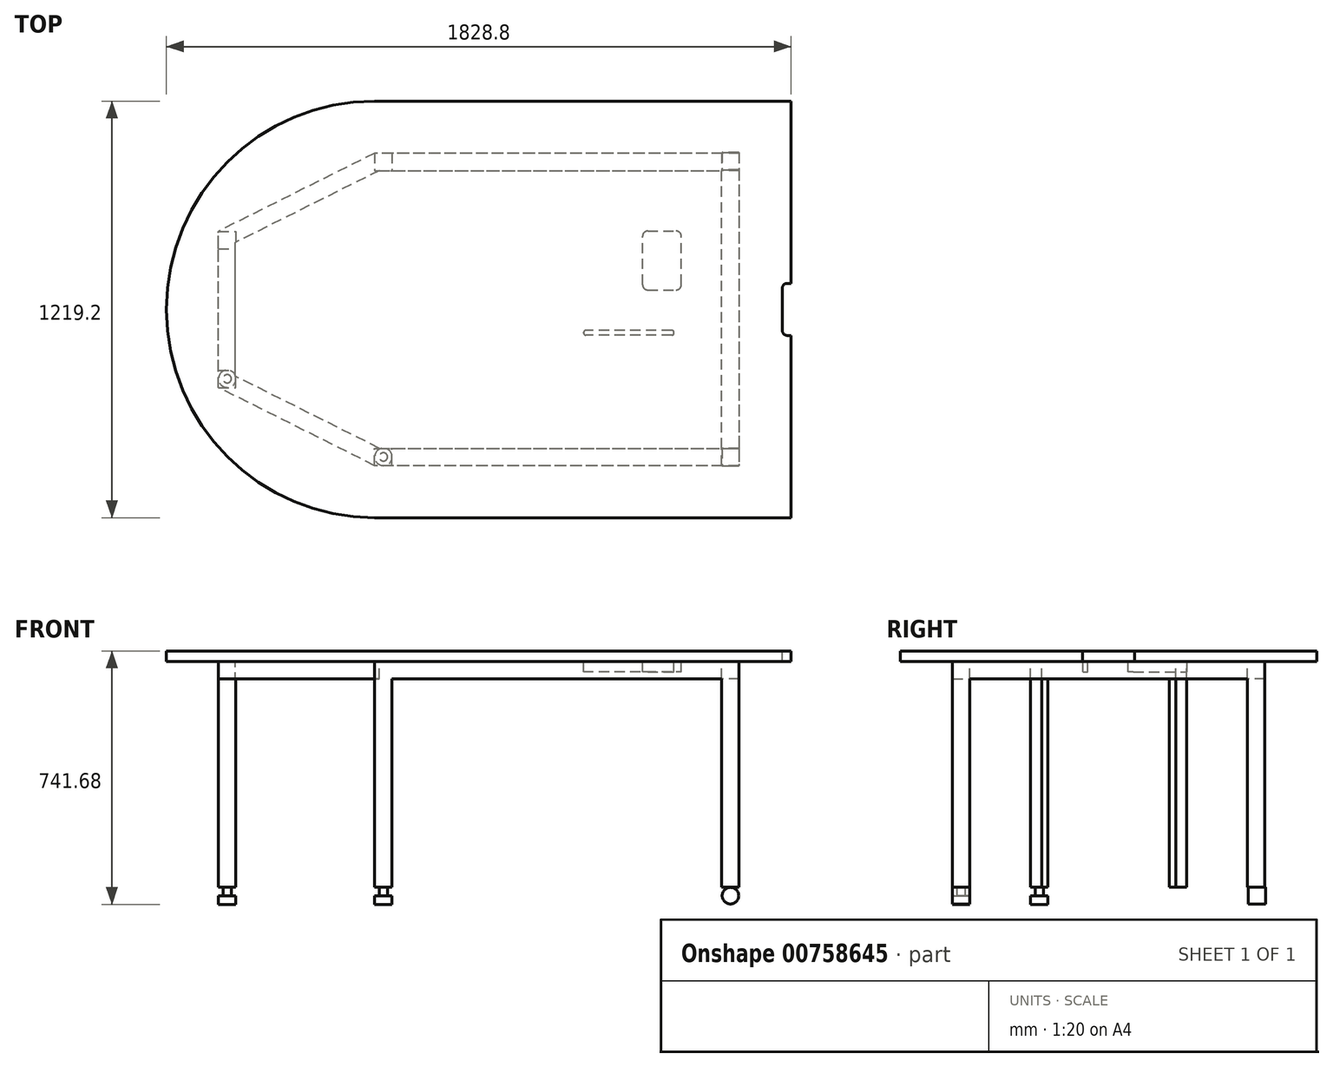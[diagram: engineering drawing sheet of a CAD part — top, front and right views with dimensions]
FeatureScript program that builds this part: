
annotation { "Feature Type Name" : "Feature", "Feature Type Description" : "" }
export const myFeature = defineFeature(function(context is Context, id is Id, definition is map)
    precondition{}
    {
        {
            var Q0;
            Q0=qCreatedBy(makeId("Top.planeOp"),FACE);
            var sketch = newSketch(context, id + "F0", { "sketchPlane" : qUnion([Q0])});
            skLineSegment(sketch, "E0.bottom", {"start": v(0, 0) * mm, "end": v(1219.2, 0) * mm});
            skLineSegment(sketch, "E0.top", {"start": v(0, -1219.2) * mm, "end": v(1219.2, -1219.2) * mm});
            skLineSegment(sketch, "E0.left", {"start": v(0, 0) * mm, "end": v(0, -1219.2) * mm});
            skCircle(sketch, "E1", {"center": v(0, -609.6) * mm, "radius": 609.6 * mm});
            skPoint(sketch, "E2.startSnap0", {"position": v(609.6, -1219.2) * mm});
            skLineSegment(sketch, "E3", {"start": v(1276.56, -609.6) * mm, "end": v(1133.94, -609.6) * mm, "construction": true});
            skPoint(sketch, "E3.startSnap0", {"position": v(1219.2, -609.6) * mm});
            skLineSegment(sketch, "E4", {"start": v(1219.2, -533.4) * mm, "end": v(1206.5, -533.4) * mm});
            skLineSegment(sketch, "E5", {"start": v(1193.8, -546.1) * mm, "end": v(1193.8, -609.6) * mm});
            skPoint(sketch, "E6.visualSharp", {"position": v(1193.8, -533.4) * mm});
            skArc(sketch, "E6.filletArc", {"start": v(1206.5, -533.4) * mm, "mid": v(1197.52, -537.12) * mm, "end": v(1193.8, -546.1) * mm});
            skLineSegment(sketch, "E7.MirrorCS", {"start": v(1193.8, -673.1) * mm, "end": v(1193.8, -609.6) * mm});
            skArc(sketch, "E8.MirrorCS", {"start": v(1206.5, -685.8) * mm, "mid": v(1197.52, -682.08) * mm, "end": v(1193.8, -673.1) * mm});
            skLineSegment(sketch, "E9.MirrorCS", {"start": v(1219.2, -685.8) * mm, "end": v(1206.5, -685.8) * mm});
            skLineSegment(sketch, "E10", {"start": v(1219.2, 0) * mm, "end": v(1219.2, -533.4) * mm});
            skLineSegment(sketch, "E11", {"start": v(1219.2, -685.8) * mm, "end": v(1219.2, -1219.2) * mm});
            skSolve(sketch);
        }
        {
            var Q0;
            {var subQ0=sQuery(id+"F0.wireOp",EDGE,"E0.bottom");Q0=makeQuery(id+"F0.imprint","IMPRINT",FACE,{"disambiguationData":[TD([[makeQuery(id+"F0.imprint","IMPRINT",EDGE,{"derivedFrom":subQ0}),-1.0]])]});}
            var Q1;
            {var subQ0=sQuery(id+"F0.wireOp",EDGE,"E0.left");Q1=makeQuery(id+"F0.imprint","IMPRINT",FACE,{"disambiguationData":[TD([[makeQuery(id+"F0.imprint","IMPRINT",EDGE,{"derivedFrom":subQ0}),-1.0]])]});}
            var Q2;
            {var subQ0=sQuery(id+"F0.wireOp",EDGE,"E0.left");Q2=makeQuery(id+"F0.imprint","IMPRINT",FACE,{"disambiguationData":[TD([[makeQuery(id+"F0.imprint","IMPRINT",EDGE,{"derivedFrom":subQ0}),1.0]])]});}
            extrude(context, id + "F1", {"entities" : qUnion([Q0, Q1, Q2]), "oppositeDirection" : true, "depth" : 30.48 * mm, "offsetDistance" : 30.48 * mm});
        }
        {
            var Q0;
            Q0=makeQuery(id+"F1.opExtrude","CAP_FACE",FACE,{"disambiguationData":[OSD([sQuery(id+"F0.wireOp",EDGE,"E0.bottom"),sQuery(id+"F0.wireOp",EDGE,"E0.top"),sQuery(id+"F0.wireOp",EDGE,"E0.right"),sQuery(id+"F0.wireOp",EDGE,"E1")])],"isStart":false});
            var sketch = newSketch(context, id + "F2", { "sketchPlane" : qUnion([Q0])});
            skPoint(sketch, "E12.startSnap0", {"position": v(1219.2, 609.6) * mm});
            skLineSegment(sketch, "E13.0", {"start": v(0, 1219.2) * mm, "end": v(1219.2, 1219.2) * mm});
            skPoint(sketch, "E14", {"position": v(0, 1066.8) * mm});
            skLineSegment(sketch, "E15", {"start": v(1066.8, 609.6) * mm, "end": v(1066.8, 1066.8) * mm});
            skLineSegment(sketch, "E16", {"start": v(1066.8, 1066.8) * mm, "end": v(0, 1066.8) * mm});
            skLineSegment(sketch, "E17", {"start": v(13.53, 1016) * mm, "end": v(1016, 1016) * mm});
            skLineSegment(sketch, "E18", {"start": v(1016, 1016) * mm, "end": v(1016, 609.6) * mm});
            skPoint(sketch, "E19", {"position": v(-457.2, 609.6) * mm});
            skPoint(sketch, "E20", {"position": v(-457.2, 838.2) * mm});
            skLineSegment(sketch, "E21", {"start": v(0, 1066.8) * mm, "end": v(-457.2, 838.2) * mm});
            skLineSegment(sketch, "E22", {"start": v(-457.2, 838.2) * mm, "end": v(-457.2, 609.6) * mm});
            skLineSegment(sketch, "E23", {"start": v(-407.87, 609.6) * mm, "end": v(-407.87, 805.3) * mm});
            skLineSegment(sketch, "E24", {"start": v(13.53, 1016) * mm, "end": v(-407.87, 805.3) * mm});
            skLineSegment(sketch, "E25.MirrorCS", {"start": v(1066.8, 609.6) * mm, "end": v(1066.8, 152.4) * mm});
            skLineSegment(sketch, "E26.MirrorCS", {"start": v(0, 152.4) * mm, "end": v(-457.2, 381) * mm});
            skLineSegment(sketch, "E27.MirrorCS", {"start": v(13.53, 203.2) * mm, "end": v(-407.87, 413.9) * mm});
            skLineSegment(sketch, "E28.MirrorCS", {"start": v(-407.87, 609.6) * mm, "end": v(-407.87, 413.9) * mm});
            skLineSegment(sketch, "E29.MirrorCS", {"start": v(-457.2, 381) * mm, "end": v(-457.2, 609.6) * mm});
            skLineSegment(sketch, "E30.MirrorCS", {"start": v(1016, 203.2) * mm, "end": v(1016, 609.6) * mm});
            skPoint(sketch, "E31.MirrorP", {"position": v(-457.2, 381) * mm});
            skLineSegment(sketch, "E32.MirrorCS", {"start": v(13.53, 203.2) * mm, "end": v(1016, 203.2) * mm});
            skLineSegment(sketch, "E33.MirrorCS", {"start": v(1066.8, 152.4) * mm, "end": v(0, 152.4) * mm});
            skSolve(sketch);
        }
        {
            var Q0;
            Q0=makeQuery(id+"F2.imprint","IMPRINT",FACE,{"disambiguationData":[TD([[makeQuery(id+"F2.imprint","IMPRINT",EDGE,{"derivedFrom":sQuery(id+"F2.wireOp",EDGE,"E15")}),1.0]])]});
            extrude(context, id + "F3", {"entities" : qUnion([Q0]), "depth" : 50.8 * mm, "offsetDistance" : 30.48 * mm});
        }
        {
            var Q0;
            Q0=makeQuery(id+"F3.opExtrude","CAP_FACE",FACE,{"disambiguationData":[OSD([sQuery(id+"F2.wireOp",EDGE,"E15"),sQuery(id+"F2.wireOp",EDGE,"E16"),sQuery(id+"F2.wireOp",EDGE,"E17"),sQuery(id+"F2.wireOp",EDGE,"E18"),sQuery(id+"F2.wireOp",EDGE,"E21"),sQuery(id+"F2.wireOp",EDGE,"E22"),sQuery(id+"F2.wireOp",EDGE,"E23"),sQuery(id+"F2.wireOp",EDGE,"E24"),sQuery(id+"F2.wireOp",EDGE,"E26.MirrorCS"),sQuery(id+"F2.wireOp",EDGE,"E27.MirrorCS"),sQuery(id+"F2.wireOp",EDGE,"E28.MirrorCS"),sQuery(id+"F2.wireOp",EDGE,"E25.MirrorCS"),sQuery(id+"F2.wireOp",EDGE,"E29.MirrorCS"),sQuery(id+"F2.wireOp",EDGE,"E30.MirrorCS"),sQuery(id+"F2.wireOp",EDGE,"E32.MirrorCS"),sQuery(id+"F2.wireOp",EDGE,"E33.MirrorCS")])],"isStart":false});
            var sketch = newSketch(context, id + "F4", { "sketchPlane" : qUnion([Q0])});
            skLineSegment(sketch, "E34.bottom", {"start": v(1066.8, 1066.8) * mm, "end": v(1016, 1066.8) * mm});
            skLineSegment(sketch, "E34.top", {"start": v(1066.8, 1016) * mm, "end": v(1016, 1016) * mm});
            skLineSegment(sketch, "E34.left", {"start": v(1066.8, 1066.8) * mm, "end": v(1066.8, 1016) * mm});
            skLineSegment(sketch, "E34.right", {"start": v(1016, 1066.8) * mm, "end": v(1016, 1016) * mm});
            skLineSegment(sketch, "E35.bottom", {"start": v(0, 1066.8) * mm, "end": v(50.8, 1066.8) * mm});
            skLineSegment(sketch, "E35.top", {"start": v(0, 1016) * mm, "end": v(50.8, 1016) * mm});
            skLineSegment(sketch, "E35.left", {"start": v(0, 1066.8) * mm, "end": v(0, 1016) * mm});
            skLineSegment(sketch, "E35.right", {"start": v(50.8, 1066.8) * mm, "end": v(50.8, 1016) * mm});
            skLineSegment(sketch, "E36.bottom", {"start": v(-457.2, 838.2) * mm, "end": v(-406.4, 838.2) * mm});
            skLineSegment(sketch, "E36.top", {"start": v(-457.2, 787.4) * mm, "end": v(-406.4, 787.4) * mm});
            skLineSegment(sketch, "E36.left", {"start": v(-457.2, 838.2) * mm, "end": v(-457.2, 787.4) * mm});
            skLineSegment(sketch, "E36.right", {"start": v(-406.4, 838.2) * mm, "end": v(-406.4, 787.4) * mm});
            skLineSegment(sketch, "E37", {"start": v(1123.66, 609.6) * mm, "end": v(-778.72, 609.6) * mm, "construction": true});
            skPoint(sketch, "E37.startSnap0", {"position": v(1066.8, 609.6) * mm});
            skLineSegment(sketch, "E38.MirrorCS", {"start": v(1066.8, 152.4) * mm, "end": v(1016, 152.4) * mm});
            skLineSegment(sketch, "E39.MirrorCS", {"start": v(1066.8, 203.2) * mm, "end": v(1016, 203.2) * mm});
            skLineSegment(sketch, "E40.MirrorCS", {"start": v(1066.8, 152.4) * mm, "end": v(1066.8, 203.2) * mm});
            skLineSegment(sketch, "E41.MirrorCS", {"start": v(1016, 152.4) * mm, "end": v(1016, 203.2) * mm});
            skLineSegment(sketch, "E42.MirrorCS", {"start": v(-406.4, 381) * mm, "end": v(-406.4, 431.8) * mm});
            skLineSegment(sketch, "E43.MirrorCS", {"start": v(-457.2, 381) * mm, "end": v(-457.2, 431.8) * mm});
            skLineSegment(sketch, "E44.MirrorCS", {"start": v(-457.2, 431.8) * mm, "end": v(-406.4, 431.8) * mm});
            skLineSegment(sketch, "E45.MirrorCS", {"start": v(0, 152.4) * mm, "end": v(50.8, 152.4) * mm});
            skLineSegment(sketch, "E46.MirrorCS", {"start": v(0, 203.2) * mm, "end": v(50.8, 203.2) * mm});
            skLineSegment(sketch, "E47.MirrorCS", {"start": v(0, 152.4) * mm, "end": v(0, 203.2) * mm});
            skLineSegment(sketch, "E48.MirrorCS", {"start": v(50.8, 152.4) * mm, "end": v(50.8, 203.2) * mm});
            skLineSegment(sketch, "E49.MirrorCS", {"start": v(-457.2, 381) * mm, "end": v(-406.4, 381) * mm});
            skSolve(sketch);
        }
        {
            var Q0;
            Q0=makeQuery(id+"F4.imprint","IMPRINT",FACE,{"disambiguationData":[TD([[makeQuery(id+"F4.imprint","IMPRINT",EDGE,{"derivedFrom":sQuery(id+"F4.wireOp",EDGE,"E35.bottom")}),1.0]])]});
            var Q1;
            Q1=makeQuery(id+"F4.imprint","IMPRINT",FACE,{"disambiguationData":[TD([[makeQuery(id+"F4.imprint","IMPRINT",EDGE,{"derivedFrom":sQuery(id+"F4.wireOp",EDGE,"E45.MirrorCS")}),-1.0]])]});
            var Q2;
            {var subQ1=sQuery(id+"F4.wireOp",EDGE,"E43.MirrorCS");Q2=makeQuery(id+"F4.imprint","IMPRINT",FACE,{"disambiguationData":[TD([[makeQuery(id+"F4.imprint","IMPRINT",EDGE,{"derivedFrom":subQ1}),1.0]])]});}
            var Q3;
            {var subQ1=sQuery(id+"F4.wireOp",EDGE,"E36.bottom");Q3=makeQuery(id+"F4.imprint","IMPRINT",FACE,{"disambiguationData":[TD([[makeQuery(id+"F4.imprint","IMPRINT",EDGE,{"derivedFrom":subQ1}),-1.0]])]});}
            extrude(context, id + "F5", {"entities" : qUnion([Q0, Q1, Q2, Q3]), "operationType" : NewBodyOperationType.ADD, "depth" : 609.6 * mm, "offsetDistance" : 30.48 * mm});
        }
        {
            var Q0;
            Q0=makeQuery(id+"F4.imprint","IMPRINT",FACE,{"disambiguationData":[TD([[makeQuery(id+"F4.imprint","IMPRINT",EDGE,{"derivedFrom":sQuery(id+"F4.wireOp",EDGE,"E34.bottom")}),1.0]])]});
            var Q1;
            Q1=makeQuery(id+"F4.imprint","IMPRINT",FACE,{"disambiguationData":[TD([[makeQuery(id+"F4.imprint","IMPRINT",EDGE,{"derivedFrom":sQuery(id+"F4.wireOp",EDGE,"E38.MirrorCS")}),-1.0]])]});
            extrude(context, id + "F6", {"entities" : qUnion([Q0, Q1]), "operationType" : NewBodyOperationType.ADD, "depth" : 609.6 * mm, "offsetDistance" : 30.48 * mm});
        }
        {
            var Q0;
            Q0=makeQuery(id+"F6.boolean.opBoolean","MERGE",FACE,{"derivedFrom":[makeQuery(id+"F5.boolean.opBoolean","MERGE",FACE,{"derivedFrom":[makeQuery(id+"F3.opExtrude","SWEPT_FACE",FACE,{"disambiguationData":[OSD([sQuery(id+"F2.wireOp",EDGE,"E16")])]}),makeQuery(id+"F5.opExtrude","SWEPT_FACE",FACE,{"disambiguationData":[OSD([sQuery(id+"F4.wireOp",EDGE,"E35.bottom")])]})]}),makeQuery(id+"F6.opExtrude","SWEPT_FACE",FACE,{"disambiguationData":[OSD([sQuery(id+"F4.wireOp",EDGE,"E34.bottom")])]})]});
            var sketch = newSketch(context, id + "F7", { "sketchPlane" : qUnion([Q0])});
            skCircle(sketch, "E50", {"center": v(1041.4, -716.23) * mm, "radius": 24.27 * mm});
            skPoint(sketch, "E50.centerSnap0", {"position": v(1041.4, -690.88) * mm});
            skSolve(sketch);
        }
        {
            var Q0;
            Q0=makeQuery(id+"F7.imprint","IMPRINT",FACE,{"disambiguationData":[TD([[makeQuery(id+"F7.imprint","IMPRINT",EDGE,{"derivedFrom":sQuery(id+"F7.wireOp",EDGE,"E50")}),1.0]])]});
            extrude(context, id + "F8", {"entities" : qUnion([Q0]), "oppositeDirection" : true, "depth" : 50.8 * mm, "offsetDistance" : 30.48 * mm});
        }
        {
            var Q0;
            Q0=makeQuery(id+"F8.opExtrude","SWEPT_BODY",BODY,{"disambiguationData":[OSD([sQuery(id+"F7.wireOp",EDGE,"E50")])]});
            transform(context, id + "F9", {"entities" : qUnion([Q0]), "transformType" : TransformType.TRANSLATION_3D, "dx" : 0 * mm, "dy" : 865.63 * mm, "dz" : 0 * mm, "makeCopy" : true});
        }
        {
            var Q0;
            Q0=makeQuery(id+"F5.opExtrude","CAP_FACE",FACE,{"disambiguationData":[OSD([sQuery(id+"F4.wireOp",EDGE,"E35.bottom"),sQuery(id+"F4.wireOp",EDGE,"E35.top"),sQuery(id+"F4.wireOp",EDGE,"E35.left"),sQuery(id+"F4.wireOp",EDGE,"E35.right")])],"isStart":false});
            var sketch = newSketch(context, id + "F10", { "sketchPlane" : qUnion([Q0])});
            skCircle(sketch, "E51", {"center": v(25.4, 1041.4) * mm, "radius": 12.23 * mm});
            skPoint(sketch, "E51.centerSnap0", {"position": v(50.8, 1041.4) * mm});
            skPoint(sketch, "E51.centerSnap1", {"position": v(25.4, 1016) * mm});
            skLineSegment(sketch, "E52.0", {"start": v(-457.2, 838.2) * mm, "end": v(-406.4, 838.2) * mm});
            skLineSegment(sketch, "E53.0", {"start": v(-457.2, 838.2) * mm, "end": v(-457.2, 787.4) * mm});
            skCircle(sketch, "E54", {"center": v(-431.8, 812.8) * mm, "radius": 12.2 * mm});
            skPoint(sketch, "E54.centerSnap0", {"position": v(-457.2, 812.8) * mm});
            skPoint(sketch, "E54.centerSnap1", {"position": v(-431.8, 838.2) * mm});
            skLineSegment(sketch, "E55.0", {"start": v(-407.87, 787.4) * mm, "end": v(-407.87, 431.8) * mm, "construction": true});
            skLineSegment(sketch, "E56", {"start": v(-520.03, 609.6) * mm, "end": v(13.37, 609.6) * mm, "construction": true});
            skPoint(sketch, "E56.startSnap0", {"position": v(-407.87, 609.6) * mm});
            skCircle(sketch, "E57.MirrorC", {"center": v(25.4, 177.8) * mm, "radius": 12.23 * mm});
            skCircle(sketch, "E58.MirrorC", {"center": v(-431.8, 406.4) * mm, "radius": 12.2 * mm});
            skSolve(sketch);
        }
        {
            var Q0;
            Q0=makeQuery(id+"F10.imprint","IMPRINT",FACE,{"disambiguationData":[TD([[makeQuery(id+"F10.imprint","IMPRINT",EDGE,{"derivedFrom":sQuery(id+"F10.wireOp",EDGE,"E51")}),1.0]])]});
            var Q1;
            Q1=makeQuery(id+"F10.imprint","IMPRINT",FACE,{"disambiguationData":[TD([[makeQuery(id+"F10.imprint","IMPRINT",EDGE,{"derivedFrom":sQuery(id+"F10.wireOp",EDGE,"E54")}),1.0]])]});
            var Q2;
            Q2=makeQuery(id+"F10.imprint","IMPRINT",FACE,{"disambiguationData":[TD([[makeQuery(id+"F10.imprint","IMPRINT",EDGE,{"derivedFrom":sQuery(id+"F10.wireOp",EDGE,"E58.MirrorC")}),-1.0]])]});
            var Q3;
            Q3=makeQuery(id+"F10.imprint","IMPRINT",FACE,{"disambiguationData":[TD([[makeQuery(id+"F10.imprint","IMPRINT",EDGE,{"derivedFrom":sQuery(id+"F10.wireOp",EDGE,"E57.MirrorC")}),-1.0]])]});
            extrude(context, id + "F11", {"entities" : qUnion([Q0, Q1, Q2, Q3]), "depth" : 25.4 * mm, "offsetDistance" : 30.48 * mm});
        }
        {
            var Q0;
            Q0=makeQuery(id+"F11.opExtrude","CAP_FACE",FACE,{"disambiguationData":[OSD([sQuery(id+"F10.wireOp",EDGE,"E51")])],"isStart":false});
            var sketch = newSketch(context, id + "F12", { "sketchPlane" : qUnion([Q0])});
            skCircle(sketch, "E59", {"center": v(25.4, 1041.4) * mm, "radius": 25.4 * mm});
            skCircle(sketch, "E60", {"center": v(-431.8, 812.8) * mm, "radius": 25.4 * mm});
            skLineSegment(sketch, "E61.0", {"start": v(-407.87, 787.4) * mm, "end": v(-407.87, 431.8) * mm, "construction": true});
            skLineSegment(sketch, "E62", {"start": v(-407.87, 609.6) * mm, "end": v(-302.85, 609.6) * mm, "construction": true});
            skCircle(sketch, "E63.MirrorC", {"center": v(-431.8, 406.4) * mm, "radius": 25.4 * mm});
            skCircle(sketch, "E64.MirrorC", {"center": v(25.4, 177.8) * mm, "radius": 25.4 * mm});
            skSolve(sketch);
        }
        {
            var Q0;
            Q0=makeQuery(id+"F12.imprint","IMPRINT",FACE,{"disambiguationData":[TD([[makeQuery(id+"F12.imprint","IMPRINT",EDGE,{"derivedFrom":sQuery(id+"F12.wireOp",EDGE,"E59")}),1.0]])]});
            var Q1;
            Q1=makeQuery(id+"F12.imprint","IMPRINT",FACE,{"disambiguationData":[TD([[makeQuery(id+"F12.imprint","IMPRINT",EDGE,{"derivedFrom":sQuery(id+"F12.wireOp",EDGE,"26092e24-e5fe-4641-b551-48940adf5273.0")}),-1.0]])]});
            var Q2;
            Q2=makeQuery(id+"F12.imprint","IMPRINT",FACE,{"disambiguationData":[TD([[makeQuery(id+"F12.imprint","IMPRINT",EDGE,{"derivedFrom":sQuery(id+"F12.wireOp",EDGE,"E63.MirrorC")}),-1.0]])]});
            var Q3;
            Q3=makeQuery(id+"F12.imprint","IMPRINT",FACE,{"disambiguationData":[TD([[makeQuery(id+"F12.imprint","IMPRINT",EDGE,{"derivedFrom":sQuery(id+"F12.wireOp",EDGE,"E64.MirrorC")}),-1.0]])]});
            var Q4;
            Q4=makeQuery(id+"F12.imprint","IMPRINT",FACE,{"disambiguationData":[TD([[makeQuery(id+"F12.imprint","IMPRINT",EDGE,{"derivedFrom":makeQuery(id+"F11.opExtrude","CAP_EDGE",EDGE,{"disambiguationData":[OSD([sQuery(id+"F10.wireOp",EDGE,"E51")])],"isStart":false})}),1.0]])]});
            var Q5;
            Q5=makeQuery(id+"F12.imprint","IMPRINT",FACE,{"disambiguationData":[TD([[makeQuery(id+"F12.imprint","IMPRINT",EDGE,{"derivedFrom":sQuery(id+"F12.wireOp",EDGE,"E60")}),1.0]])]});
            extrude(context, id + "F13", {"entities" : qUnion([Q0, Q1, Q2, Q3, Q4, Q5]), "depth" : 25.4 * mm, "offsetDistance" : 30.48 * mm});
        }
        {
            var Q0;
            Q0=makeQuery(id+"F1.opExtrude","CAP_FACE",FACE,{"disambiguationData":[OSD([sQuery(id+"F0.wireOp",EDGE,"E0.bottom"),sQuery(id+"F0.wireOp",EDGE,"E0.top"),sQuery(id+"F0.wireOp",EDGE,"E1"),sQuery(id+"F0.wireOp",EDGE,"E4"),sQuery(id+"F0.wireOp",EDGE,"E5"),sQuery(id+"F0.wireOp",EDGE,"E6.filletArc"),sQuery(id+"F0.wireOp",EDGE,"E7.MirrorCS"),sQuery(id+"F0.wireOp",EDGE,"E8.MirrorCS"),sQuery(id+"F0.wireOp",EDGE,"E9.MirrorCS"),sQuery(id+"F0.wireOp",EDGE,"E10"),sQuery(id+"F0.wireOp",EDGE,"E11")])],"isStart":false});
            var sketch = newSketch(context, id + "F14", { "sketchPlane" : qUnion([Q0])});
            skLineSegment(sketch, "E65.bottom", {"start": v(798.98, 552.69) * mm, "end": v(882.38, 552.69) * mm});
            skLineSegment(sketch, "E65.top", {"start": v(798.98, 380.6) * mm, "end": v(882.38, 380.6) * mm});
            skLineSegment(sketch, "E65.left", {"start": v(783.74, 537.45) * mm, "end": v(783.74, 395.83) * mm});
            skLineSegment(sketch, "E65.right", {"start": v(897.62, 537.45) * mm, "end": v(897.62, 395.83) * mm});
            skPoint(sketch, "E66.visualSharp", {"position": v(783.74, 552.69) * mm});
            skArc(sketch, "E66.filletArc", {"start": v(798.98, 552.69) * mm, "mid": v(788.2, 548.22) * mm, "end": v(783.74, 537.45) * mm});
            skPoint(sketch, "E67.visualSharp", {"position": v(897.62, 552.69) * mm});
            skArc(sketch, "E67.filletArc", {"start": v(897.62, 537.45) * mm, "mid": v(893.15, 548.22) * mm, "end": v(882.38, 552.69) * mm});
            skPoint(sketch, "E68.visualSharp", {"position": v(897.62, 380.6) * mm});
            skArc(sketch, "E68.filletArc", {"start": v(882.38, 380.6) * mm, "mid": v(893.15, 385.06) * mm, "end": v(897.62, 395.83) * mm});
            skPoint(sketch, "E69.visualSharp", {"position": v(783.74, 380.6) * mm});
            skArc(sketch, "E69.filletArc", {"start": v(783.74, 395.83) * mm, "mid": v(788.2, 385.06) * mm, "end": v(798.98, 380.6) * mm});
            skLineSegment(sketch, "E70.bottom", {"start": v(870, 684.93) * mm, "end": v(617.7, 684.93) * mm});
            skLineSegment(sketch, "E70.top", {"start": v(870, 671.35) * mm, "end": v(617.7, 671.35) * mm});
            skLineSegment(sketch, "E70.left", {"start": v(876.1, 678.83) * mm, "end": v(876.1, 677.45) * mm});
            skLineSegment(sketch, "E70.right", {"start": v(611.6, 678.83) * mm, "end": v(611.6, 677.45) * mm});
            skPoint(sketch, "E71.visualSharp", {"position": v(611.6, 684.93) * mm});
            skArc(sketch, "E71.filletArc", {"start": v(617.7, 684.93) * mm, "mid": v(613.39, 683.14) * mm, "end": v(611.6, 678.83) * mm});
            skPoint(sketch, "E72.visualSharp", {"position": v(876.1, 684.93) * mm});
            skArc(sketch, "E72.filletArc", {"start": v(876.1, 678.83) * mm, "mid": v(874.32, 683.14) * mm, "end": v(870, 684.93) * mm});
            skPoint(sketch, "E73.visualSharp", {"position": v(611.6, 671.35) * mm});
            skArc(sketch, "E73.filletArc", {"start": v(611.6, 677.45) * mm, "mid": v(613.39, 673.14) * mm, "end": v(617.7, 671.35) * mm});
            skPoint(sketch, "E74.visualSharp", {"position": v(876.1, 671.35) * mm});
            skArc(sketch, "E74.filletArc", {"start": v(870, 671.35) * mm, "mid": v(874.32, 673.14) * mm, "end": v(876.1, 677.45) * mm});
            skSolve(sketch);
        }
        {
            var Q0;
            Q0=makeQuery(id+"F14.imprint","IMPRINT",FACE,{"disambiguationData":[TD([[makeQuery(id+"F14.imprint","IMPRINT",EDGE,{"derivedFrom":sQuery(id+"F14.wireOp",EDGE,"E70.bottom")}),1.0]])]});
            var Q1;
            Q1=makeQuery(id+"F14.imprint","IMPRINT",FACE,{"disambiguationData":[TD([[makeQuery(id+"F14.imprint","IMPRINT",EDGE,{"derivedFrom":sQuery(id+"F14.wireOp",EDGE,"E65.bottom")}),-1.0]])]});
            extrude(context, id + "F15", {"entities" : qUnion([Q0, Q1]), "depth" : 30.48 * mm, "offsetDistance" : 30.48 * mm});
        }
    });
